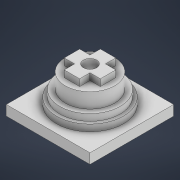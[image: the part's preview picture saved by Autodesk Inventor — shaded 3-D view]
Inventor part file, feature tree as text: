
AUTODESK INVENTOR PART (.ipt)
format: ipt  version: 2021 (Build 250183000, 183)  size: 322,560 bytes
history: native  units: mm
features: extrude x7, sketch x7
ambient origin geometry x8: Origin, YZ Plane, XZ Plane, XY Plane, X Axis, Y Axis, Z Axis, Center Point
bodies: Volumenkörper1 (feature_tree)
feature tree (14):
  extrude  "Extrusion1"  Depth=2.0mm TaperAngle=0.0deg
  extrude  "Extrusion2"  Depth=2.0mm TaperAngle=0.0deg
  extrude  "Extrusion3"  Depth=4.5mm TaperAngle=0.0deg
  extrude  "Extrusion4"  Depth=10.8mm
  extrude  "Extrusion5"  Depth=3.1mm
  extrude  "Extrusion6"  Depth=3.1mm
  extrude  "Extrusion7"  Depth=3.1mm
  sketch  "Skizze1"  dims[d0=20.0mm d1=2.0mm d2=0.0mm]
  sketch  "Skizze2"  dims[d3=18.0mm d4=2.0mm d5=0.0mm]
  sketch  "Skizze3"  dims[d6=14.7mm d7=4.5mm d8=0.0mm]
  sketch  "Skizze4"  dims[d9=10.8mm d10=10.8mm]
  sketch  "Skizze5"  dims[d11=3.1mm d12=3.1mm]
  sketch  "Skizze6"  dims[d13=3.1mm d14=3.1mm]
  sketch  "Skizze7"  dims[d15=3.1mm d16=3.1mm d17=3.1mm d18=3.1mm d19=2.0mm d20=0.0mm d21=4.0mm d22=5.0mm d23=0.0mm d24=25.0mm d25=25.0mm d26=3.0mm d27=0.0mm d28=4.0mm d29=5.0mm d30=0.0mm]
